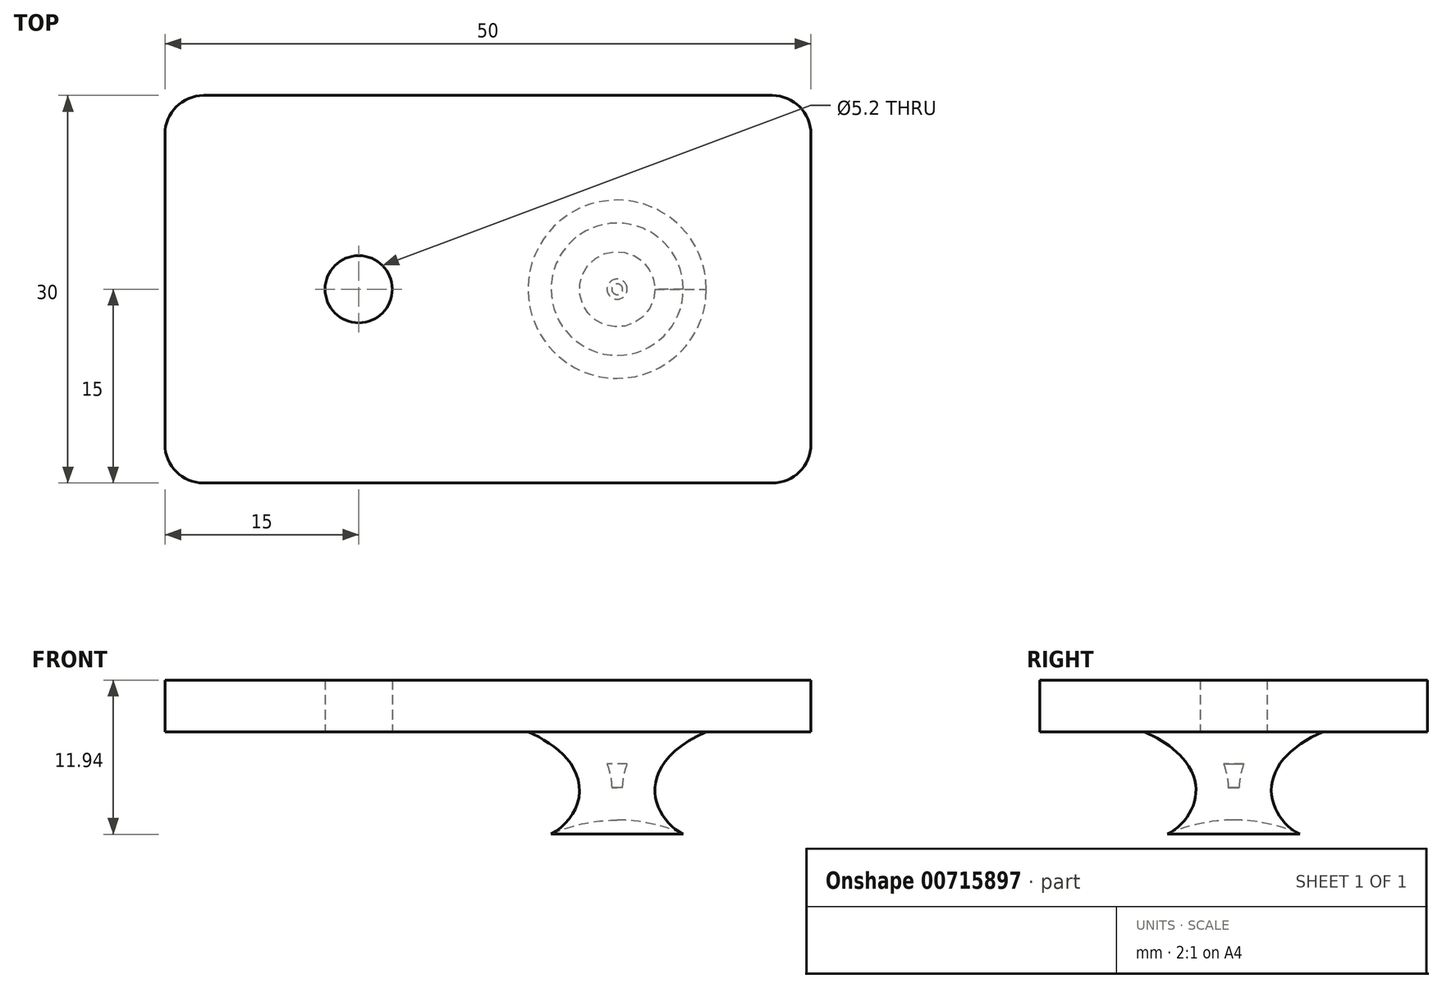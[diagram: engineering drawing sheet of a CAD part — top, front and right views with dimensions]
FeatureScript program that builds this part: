
annotation { "Feature Type Name" : "Feature", "Feature Type Description" : "" }
export const myFeature = defineFeature(function(context is Context, id is Id, definition is map)
    precondition{}
    {
        {
            var Q0;
            Q0=qCreatedBy(makeId("Front.planeOp"),FACE);
            var sketch = newSketch(context, id + "F0", { "sketchPlane" : qUnion([Q0])});
            skLineSegment(sketch, "E0", {"start": v(0, 0) * mm, "end": v(0, -36.84) * mm});
            skArc(sketch, "E1", {"start": v(0, -11.84) * mm, "mid": v(-12.5, -24.34) * mm, "end": v(0, -36.84) * mm});
            skLineSegment(sketch, "E2", {"start": v(0, -5) * mm, "end": v(-6.9, -5) * mm});
            skLineSegment(sketch, "E3", {"start": v(0, -13) * mm, "end": v(-5.25, -13) * mm, "construction": true});
            skFitSpline(sketch, "E4", {"points": [v(-5.25, -13) * mm, v(-6.9, -5) * mm], "startDerivative": vector(7.3, 3.37) * mm, "endDerivative": vector(-17.96, 8.1) * mm});
            skSolve(sketch);
        }
        {
            var Q0;
            {var subQ0=sQuery(id+"F0.wireOp",EDGE,"E1");var subQ1=sQuery(id+"F0.wireOp",EDGE,"E0");var subQ2=makeQuery(id+"F0.imprint","INTERSECT",VERTEX,{"disambiguationData":[OD(0.0)],"derivedFrom":[subQ1,subQ0]});Q0=makeQuery(id+"F0.imprint","IMPRINT",FACE,{"disambiguationData":[TD([[makeQuery(id+"F0.imprint","IMPRINT",EDGE,{"disambiguationData":[TD([[subQ2,1.0]])],"derivedFrom":subQ1}),-1.0]])]});}
            var Q1;
            {var subQ3=sQuery(id+"F0.wireOp",EDGE,"E2");Q1=makeQuery(id+"F0.imprint","IMPRINT",FACE,{"disambiguationData":[TD([[makeQuery(id+"F0.imprint","IMPRINT",EDGE,{"derivedFrom":subQ3}),1.0]])]});}
            var Q2;
            Q2=sQuery(id+"F0.wireOp",EDGE,"E0");
            revolve(context, id + "F1", {"entities" : qUnion([Q0, Q1]), "axis" : qUnion([Q2]), "revolveType" : RevolveType.FULL});
        }
        {
            var Q0;
            Q0=makeQuery(id+"F1.opRevolve","SWEPT_FACE",FACE,{"disambiguationData":[OSD([sQuery(id+"F0.wireOp",EDGE,"E1")])]});
            var Q1;
            Q1=makeQuery(id+"F1.opRevolve","SWEPT_FACE",FACE,{"disambiguationData":[OSD([sQuery(id+"F0.wireOp",EDGE,"E4")])]});
            var Q2;
            Q2=makeQuery(id+"F1.opRevolve","SWEPT_BODY",BODY,{"disambiguationData":[OSD([sQuery(id+"F0.wireOp",EDGE,"E0"),sQuery(id+"F0.wireOp",EDGE,"E1"),sQuery(id+"F0.wireOp",EDGE,"E2"),sQuery(id+"F0.wireOp",EDGE,"E4")])]});
            shell(context, id + "F2", {"isHollow" : true, "entities" : qUnion([Q0, Q1]), "parts" : qUnion([Q2]), "thickness" : 2.5 * mm});
        }
        {
            var Q0;
            Q0=makeQuery(id+"F1.opRevolve","SWEPT_FACE",FACE,{"disambiguationData":[OSD([sQuery(id+"F0.wireOp",EDGE,"E2")])]});
            var sketch = newSketch(context, id + "F3", { "sketchPlane" : qUnion([Q0])});
            skPoint(sketch, "E5", {"position": v(0, 0) * mm});
            skLineSegment(sketch, "E6.bottom", {"start": v(12, -15) * mm, "end": v(-32, -15) * mm});
            skLineSegment(sketch, "E6.top", {"start": v(12, 15) * mm, "end": v(-32, 15) * mm});
            skLineSegment(sketch, "E6.left", {"start": v(15, -12) * mm, "end": v(15, 12) * mm});
            skLineSegment(sketch, "E6.right", {"start": v(-35, -12) * mm, "end": v(-35, 12) * mm});
            skPoint(sketch, "E7.visualSharp", {"position": v(15, -15) * mm});
            skArc(sketch, "E7.filletArc", {"start": v(12, -15) * mm, "mid": v(14.12, -14.12) * mm, "end": v(15, -12) * mm});
            skPoint(sketch, "E8.visualSharp", {"position": v(15, 15) * mm});
            skArc(sketch, "E8.filletArc", {"start": v(15, 12) * mm, "mid": v(14.12, 14.12) * mm, "end": v(12, 15) * mm});
            skPoint(sketch, "E9.visualSharp", {"position": v(-35, 15) * mm});
            skArc(sketch, "E9.filletArc", {"start": v(-32, 15) * mm, "mid": v(-34.12, 14.12) * mm, "end": v(-35, 12) * mm});
            skPoint(sketch, "E10.visualSharp", {"position": v(-35, -15) * mm});
            skArc(sketch, "E10.filletArc", {"start": v(-35, -12) * mm, "mid": v(-34.12, -14.12) * mm, "end": v(-32, -15) * mm});
            skCircle(sketch, "E11", {"center": v(-20, 0) * mm, "radius": 2.6 * mm});
            skSolve(sketch);
        }
        {
            var Q0;
            Q0=qSketchRegion(id+"F3",true);
            extrude(context, id + "F4", {"entities" : qUnion([Q0]), "operationType" : NewBodyOperationType.ADD, "depth" : 4 * mm});
        }
    });
